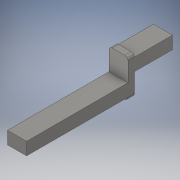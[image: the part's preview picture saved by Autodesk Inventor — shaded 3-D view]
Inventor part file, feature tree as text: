
AUTODESK INVENTOR PART (.ipt)
format: ipt  version: 2018 (Build 220112000, 112)  size: 155,136 bytes
history: native  units: in
note: dims shown in document units (in); Inventor stores cm internally (conversion verified against a paired STEP export)
features: extrude x5, sketch x5, fillet x1
ambient origin geometry x8: Origin, YZ Plane, XZ Plane, XY Plane, X Axis, Y Axis, Z Axis, Center Point
bodies: Solid1 (feature_tree)
feature tree (11):
  extrude  "Extrusion1"  Depth=2.875in
  extrude  "Extrusion2"  Depth=2.0in
  extrude  "Extrusion3"  Depth=0.375in TaperAngle=0.0deg
  extrude  "Extrusion4"  Depth=0.3125in
  extrude  "Extrusion5"  Depth=2.0in
  fillet  "Fillet1"  Radius=0.0625in
  sketch  "Sketch1"  dims[d0=0.75in d1=2.875in]
  sketch  "Sketch2"  dims[d2=0.375in d3=0.0in d4=2.0in]
  sketch  "Sketch3"  dims[d6=0.3125in d7=0.375in d8=0.0in]
  sketch  "Sketch4"  dims[d9=0.125in d10=0.3125in]
  sketch  "Sketch5"  dims[d11=0.375in d12=0.0in d13=2.0in d14=0.0625in d15=0.375in d16=0.0in d17=0.75in d18=0.0625in d19=0.375in d20=0.0in d31=0.0625in]
